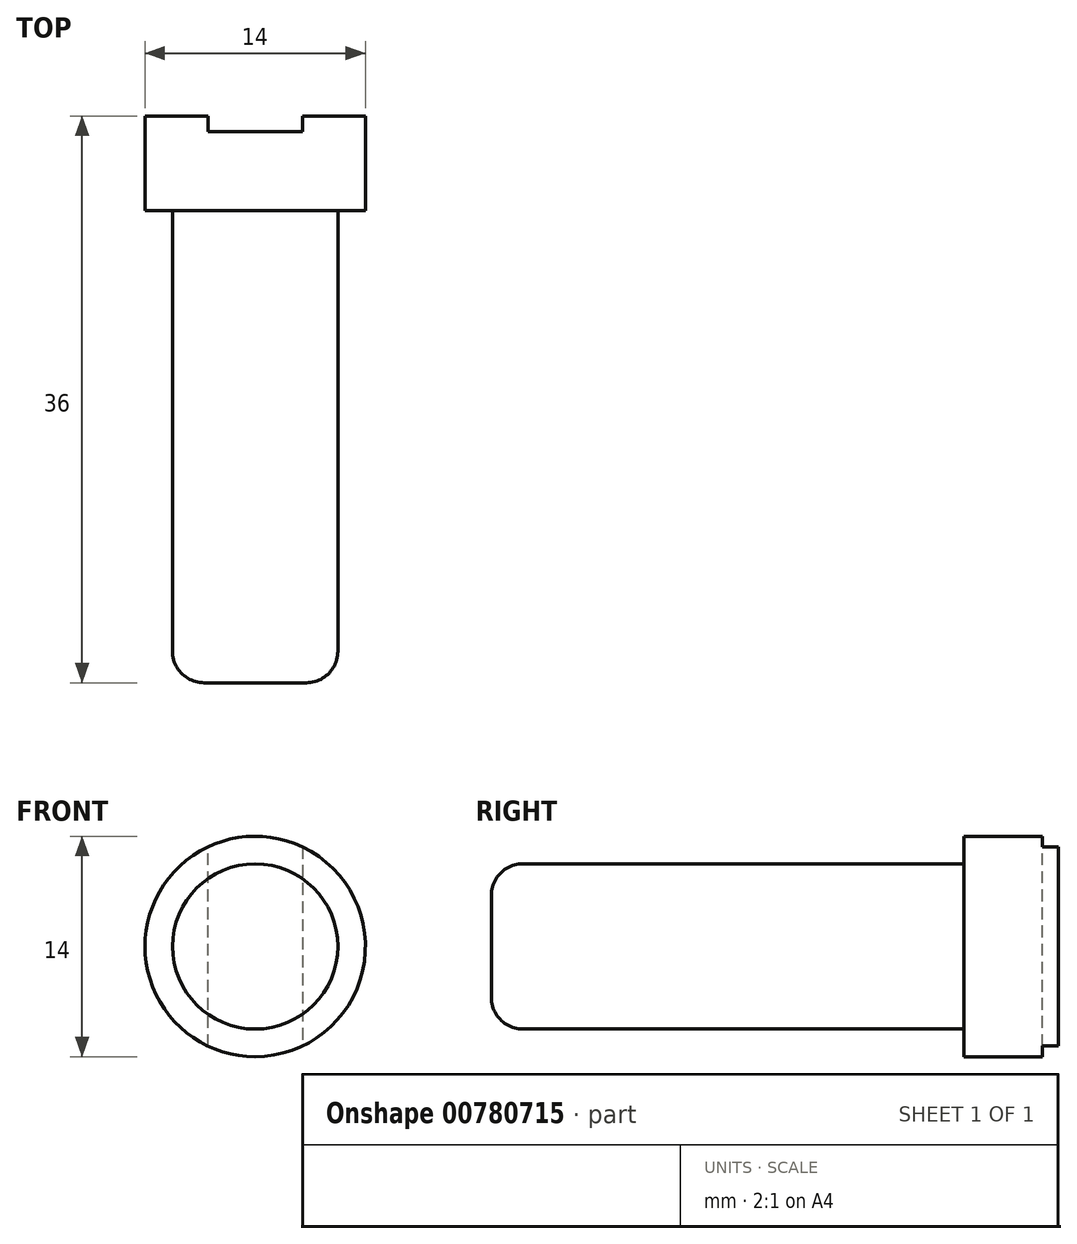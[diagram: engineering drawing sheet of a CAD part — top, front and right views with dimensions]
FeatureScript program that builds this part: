
annotation { "Feature Type Name" : "Feature", "Feature Type Description" : "" }
export const myFeature = defineFeature(function(context is Context, id is Id, definition is map)
    precondition{}
    {
        {
            var Q0;
            Q0=qCreatedBy(makeId("Front.planeOp"),FACE);
            var sketch = newSketch(context, id + "F0", { "sketchPlane" : qUnion([Q0])});
            skCircle(sketch, "E0", {"center": v(0, 0) * mm, "radius": 7 * mm});
            skSolve(sketch);
        }
        {
            var Q0;
            Q0=makeQuery(id+"F0.imprint","IMPRINT",FACE,{"disambiguationData":[TD([[makeQuery(id+"F0.imprint","IMPRINT",EDGE,{"derivedFrom":sQuery(id+"F0.wireOp",EDGE,"E0")}),1.0]])]});
            extrude(context, id + "F1", {"entities" : qUnion([Q0]), "depth" : 6 * mm, "offsetDistance" : 25 * mm});
        }
        {
            var Q0;
            Q0=makeQuery(id+"F1.opExtrude","CAP_FACE",FACE,{"disambiguationData":[OSD([sQuery(id+"F0.wireOp",EDGE,"E0")])],"isStart":false});
            var sketch = newSketch(context, id + "F2", { "sketchPlane" : qUnion([Q0])});
            skCircle(sketch, "E1", {"center": v(0, 0) * mm, "radius": 5.25 * mm});
            skSolve(sketch);
        }
        {
            var Q0;
            Q0=makeQuery(id+"F2.imprint","IMPRINT",FACE,{"disambiguationData":[TD([[makeQuery(id+"F2.imprint","IMPRINT",EDGE,{"derivedFrom":sQuery(id+"F2.wireOp",EDGE,"E1")}),1.0]])]});
            extrude(context, id + "F3", {"entities" : qUnion([Q0]), "operationType" : NewBodyOperationType.ADD, "depth" : 30 * mm, "offsetDistance" : 25 * mm});
        }
        {
            var Q0;
            Q0=makeQuery(id+"F1.opExtrude","CAP_FACE",FACE,{"disambiguationData":[OSD([sQuery(id+"F0.wireOp",EDGE,"E0")])],"isStart":true});
            var sketch = newSketch(context, id + "F4", { "sketchPlane" : qUnion([Q0])});
            skPoint(sketch, "E2", {"position": v(-3, 0) * mm});
            skPoint(sketch, "E3", {"position": v(3, 0) * mm});
            skLineSegment(sketch, "E4", {"start": v(-3, 9.51) * mm, "end": v(-3, -11.14) * mm});
            skLineSegment(sketch, "E5", {"start": v(-3, -11.14) * mm, "end": v(3, -11.14) * mm});
            skLineSegment(sketch, "E6", {"start": v(3, -11.14) * mm, "end": v(3, 9.51) * mm});
            skLineSegment(sketch, "E7", {"start": v(3, 9.51) * mm, "end": v(-2.47, 9.51) * mm});
            skLineSegment(sketch, "E8", {"start": v(-2.47, 9.51) * mm, "end": v(-3, 9.51) * mm});
            skSolve(sketch);
        }
        {
            var Q0;
            {var subQ1=sQuery(id+"F4.wireOp",EDGE,"E7");Q0=makeQuery(id+"F4.imprint","IMPRINT",FACE,{"disambiguationData":[TD([[makeQuery(id+"F4.imprint","IMPRINT",EDGE,{"derivedFrom":subQ1}),1.0]])]});}
            var Q1;
            {var subQ0=sQuery(id+"F4.wireOp",EDGE,"E5");Q1=makeQuery(id+"F4.imprint","IMPRINT",FACE,{"disambiguationData":[TD([[makeQuery(id+"F4.imprint","IMPRINT",EDGE,{"derivedFrom":subQ0}),1.0]])]});}
            var Q2;
            {var subQ0=sQuery(id+"F4.wireOp",EDGE,"E4");var subQ1=makeQuery(id+"F1.opExtrude","CAP_EDGE",EDGE,{"disambiguationData":[OSD([sQuery(id+"F0.wireOp",EDGE,"E0")])],"isStart":true});var subQ2=makeQuery(id+"F4.imprint","INTERSECT",VERTEX,{"disambiguationData":[OD(0.0)],"derivedFrom":[subQ1,subQ0]});Q2=makeQuery(id+"F4.imprint","IMPRINT",FACE,{"disambiguationData":[TD([[makeQuery(id+"F4.imprint","IMPRINT",EDGE,{"disambiguationData":[TD([[subQ2,-1.0]])],"derivedFrom":subQ0}),1.0]])]});}
            extrude(context, id + "F5", {"entities" : qUnion([Q0, Q1, Q2]), "operationType" : NewBodyOperationType.REMOVE, "oppositeDirection" : true, "depth" : 1 * mm, "offsetDistance" : 25 * mm});
        }
        {
            var Q0;
            Q0=makeQuery(id+"F3.opExtrude","CAP_EDGE",EDGE,{"disambiguationData":[OSD([sQuery(id+"F2.wireOp",EDGE,"E1")])],"isStart":false});
            fillet(context, id + "F6", {"entities" : qUnion([Q0]), "radius" : 2 * mm, "tangentPropagation" : true, "allowEdgeOverflow" : false});
        }
    });
